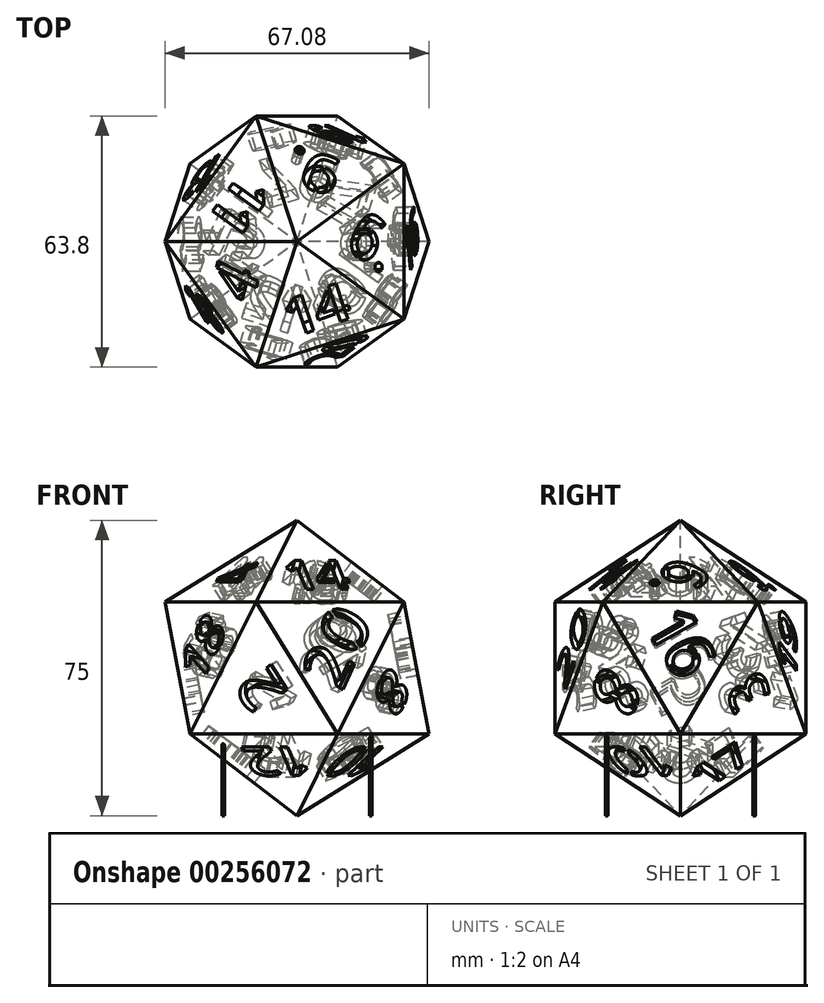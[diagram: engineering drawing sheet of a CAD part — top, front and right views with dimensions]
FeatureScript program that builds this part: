
annotation { "Feature Type Name" : "Feature", "Feature Type Description" : "" }
export const myFeature = defineFeature(function(context is Context, id is Id, definition is map)
    precondition{}
    {
        {
            var Q0;
            Q0=qCreatedBy(makeId("Front.planeOp"),FACE);
            var sketch = newSketch(context, id + "F0", { "sketchPlane" : qUnion([Q0])});
            skCircle(sketch, "E0", {"center": v(0, 0) * mm, "radius": 25 * mm, "construction": true});
            skLineSegment(sketch, "E1", {"start": v(0, 25) * mm, "end": v(-22.36, 11.18) * mm});
            skLineSegment(sketch, "E2", {"start": v(-22.36, 11.18) * mm, "end": v(-18.1, -11.18) * mm});
            skLineSegment(sketch, "E3", {"start": v(-18.1, -11.18) * mm, "end": v(0, -25) * mm});
            skLineSegment(sketch, "E4", {"start": v(0, -25) * mm, "end": v(22.36, -11.18) * mm});
            skLineSegment(sketch, "E5", {"start": v(22.36, -11.18) * mm, "end": v(18.1, 11.18) * mm});
            skLineSegment(sketch, "E6", {"start": v(0, 25) * mm, "end": v(18.1, 11.18) * mm});
            skCircle(sketch, "E7", {"center": v(0, 0) * mm, "radius": 15.18 * mm, "construction": true});
            skLineSegment(sketch, "E8", {"start": v(0, 15.18) * mm, "end": v(-13.14, -7.59) * mm, "construction": true});
            skLineSegment(sketch, "E9", {"start": v(-13.14, -7.59) * mm, "end": v(13.14, -7.59) * mm, "construction": true});
            skLineSegment(sketch, "E10", {"start": v(13.14, -7.59) * mm, "end": v(0, 15.18) * mm, "construction": true});
            skLineSegment(sketch, "E11", {"start": v(0, -7.59) * mm, "end": v(0, 15.18) * mm, "construction": true});
            skLineSegment(sketch, "E12", {"start": v(13.14, -7.59) * mm, "end": v(0, 0) * mm, "construction": true});
            skLineSegment(sketch, "E13", {"start": v(0, 0) * mm, "end": v(12.06, 15.79) * mm, "construction": true});
            skLineSegment(sketch, "E14", {"start": v(0, 0) * mm, "end": v(-12.06, 9.21) * mm, "construction": true});
            skLineSegment(sketch, "E15", {"start": v(0, 25) * mm, "end": v(-12.06, 9.21) * mm, "construction": true});
            skSolve(sketch);
        }
        {
            var Q0;
            Q0=sQuery(id+"F0.wireOp",EDGE,"E6");
            var Q1;
            Q1=qCreatedBy(makeId("Front.planeOp"),FACE);
            cPlane(context, id + "F1", {"entities" : qUnion([Q0, Q1]), "cplaneType" : CPlaneType.LINE_ANGLE, "offset" : 25 * mm, "angle" : 90 * degree, "width" : 150 * mm, "height" : 150 * mm});
        }
        {
            var Q0;
            Q0=qCreatedBy(id+"F1.planeOp",FACE);
            var sketch = newSketch(context, id + "F2", { "sketchPlane" : qUnion([Q0])});
            skLineSegment(sketch, "E16", {"start": v(-15.18, 0) * mm, "end": v(7.59, 13.14) * mm});
            skLineSegment(sketch, "E17", {"start": v(7.59, 13.14) * mm, "end": v(7.59, -13.14) * mm});
            skLineSegment(sketch, "E18", {"start": v(7.59, -13.14) * mm, "end": v(-15.18, 0) * mm});
            skSolve(sketch);
        }
        {
            var Q0;
            Q0=qSketchRegion(id+"F2",true);
            var Q1;
            Q1=sQuery(id+"F0.wireOp",VERTEX,"E12.end");
            loft(context, id + "F3", {"sheetProfilesArray" : [{ "sheetProfileEntities" : qUnion([Q0]) }, { "sheetProfileEntities" : qUnion([Q1]) }]});
        }
        {
            var Q0;
            Q0=makeQuery(id+"F3.opLoft","SWEPT_BODY",BODY,{"disambiguationData":[OSD([sQuery(id+"F0.wireOp",VERTEX,"E12.end"),makeQuery(id+"F2.imprint","IMPRINT",FACE,{"disambiguationData":[TD([[makeQuery(id+"F2.imprint","IMPRINT",EDGE,{"derivedFrom":sQuery(id+"F2.wireOp",EDGE,"E16")}),-1.0]])]})])]});
            var Q1;
            {var subQ0=sQuery(id+"F2.wireOp",EDGE,"E17");var subQ1=sQuery(id+"F2.wireOp",EDGE,"E18");var subQ2=sQuery(id+"F2.wireOp",EDGE,"E16");Q1=makeQuery(id+"F3.opLoft","SWEPT_FACE",FACE,{"disambiguationData":[OSD([subQ2,subQ0,subQ1]),TDD([makeQuery(id+"F2.imprint","INTERSECT",VERTEX,{"derivedFrom":[subQ2,subQ0]}),makeQuery(id+"F2.imprint","INTERSECT",VERTEX,{"derivedFrom":[subQ0,subQ1]}),makeQuery(id+"F2.imprint","IMPRINT",EDGE,{"derivedFrom":subQ0})])]});}
            mirror(context, id + "F4", {"entities" : qUnion([Q0]), "mirrorPlane" : qUnion([Q1])});
        }
        {
            var Q0;
            Q0=makeQuery(id+"F4.opPattern","COPY",BODY,{"derivedFrom":makeQuery(id+"F3.opLoft","SWEPT_BODY",BODY,{"disambiguationData":[OSD([sQuery(id+"F0.wireOp",VERTEX,"E12.end"),makeQuery(id+"F2.imprint","IMPRINT",FACE,{"disambiguationData":[TD([[makeQuery(id+"F2.imprint","IMPRINT",EDGE,{"derivedFrom":sQuery(id+"F2.wireOp",EDGE,"E16")}),-1.0]])]})])]}),"instanceName":"1"});
            var Q1;
            {var subQ0=sQuery(id+"F2.wireOp",EDGE,"E16");var subQ1=sQuery(id+"F2.wireOp",EDGE,"E17");var subQ2=sQuery(id+"F2.wireOp",EDGE,"E18");Q1=makeQuery(id+"F4.opPattern","COPY",FACE,{"derivedFrom":makeQuery(id+"F3.opLoft","SWEPT_FACE",FACE,{"disambiguationData":[OSD([subQ0,subQ1,subQ2]),TDD([makeQuery(id+"F2.imprint","INTERSECT",VERTEX,{"derivedFrom":[subQ0,subQ2]}),makeQuery(id+"F2.imprint","INTERSECT",VERTEX,{"derivedFrom":[subQ0,subQ1]}),makeQuery(id+"F2.imprint","IMPRINT",EDGE,{"derivedFrom":subQ0})])]}),"instanceName":"1"});}
            mirror(context, id + "F5", {"entities" : qUnion([Q0]), "mirrorPlane" : qUnion([Q1])});
        }
        {
            var Q0;
            Q0=makeQuery(id+"F4.opPattern","COPY",BODY,{"derivedFrom":makeQuery(id+"F3.opLoft","SWEPT_BODY",BODY,{"disambiguationData":[OSD([sQuery(id+"F0.wireOp",VERTEX,"E12.end"),makeQuery(id+"F2.imprint","IMPRINT",FACE,{"disambiguationData":[TD([[makeQuery(id+"F2.imprint","IMPRINT",EDGE,{"derivedFrom":sQuery(id+"F2.wireOp",EDGE,"E16")}),-1.0]])]})])]}),"instanceName":"1"});
            var Q1;
            Q1=makeQuery(id+"F5.opPattern","COPY",BODY,{"derivedFrom":makeQuery(id+"F4.opPattern","COPY",BODY,{"derivedFrom":makeQuery(id+"F3.opLoft","SWEPT_BODY",BODY,{"disambiguationData":[OSD([sQuery(id+"F0.wireOp",VERTEX,"E12.end"),makeQuery(id+"F2.imprint","IMPRINT",FACE,{"disambiguationData":[TD([[makeQuery(id+"F2.imprint","IMPRINT",EDGE,{"derivedFrom":sQuery(id+"F2.wireOp",EDGE,"E16")}),-1.0]])]})])]}),"instanceName":"1"}),"instanceName":"1"});
            var Q2;
            Q2=makeQuery(id+"F3.opLoft","SWEPT_EDGE",EDGE,{"disambiguationData":[OSD([sQuery(id+"F0.wireOp",VERTEX,"E12.end"),sQuery(id+"F2.wireOp",EDGE,"E16"),sQuery(id+"F2.wireOp",EDGE,"E18")])]});
            circularPattern(context, id + "F6", {"entities" : qUnion([Q0, Q1]), "axis" : qUnion([Q2]), "angle" : 72 * degree, "instanceCount" : 5});
        }
        {
            var Q0;
            Q0=makeQuery(id+"F3.opLoft","SWEPT_BODY",BODY,{"disambiguationData":[OSD([sQuery(id+"F0.wireOp",VERTEX,"E12.end"),makeQuery(id+"F2.imprint","IMPRINT",FACE,{"disambiguationData":[TD([[makeQuery(id+"F2.imprint","IMPRINT",EDGE,{"derivedFrom":sQuery(id+"F2.wireOp",EDGE,"E16")}),-1.0]])]})])]});
            var Q1;
            Q1=makeQuery(id+"F3.opLoft","SWEPT_EDGE",EDGE,{"disambiguationData":[OSD([sQuery(id+"F0.wireOp",VERTEX,"E12.end"),sQuery(id+"F2.wireOp",EDGE,"E16"),sQuery(id+"F2.wireOp",EDGE,"E18")])]});
            circularPattern(context, id + "F7", {"entities" : qUnion([Q0]), "axis" : qUnion([Q1]), "angle" : 72 * degree, "instanceCount" : 5});
        }
        {
            var Q0;
            Q0=makeQuery(id+"F7.opPattern","COPY",BODY,{"derivedFrom":makeQuery(id+"F3.opLoft","SWEPT_BODY",BODY,{"disambiguationData":[OSD([sQuery(id+"F0.wireOp",VERTEX,"E12.end"),makeQuery(id+"F2.imprint","IMPRINT",FACE,{"disambiguationData":[TD([[makeQuery(id+"F2.imprint","IMPRINT",EDGE,{"derivedFrom":sQuery(id+"F2.wireOp",EDGE,"E16")}),-1.0]])]})])]}),"instanceName":"4"});
            var Q1;
            Q1=makeQuery(id+"F3.opLoft","SWEPT_BODY",BODY,{"disambiguationData":[OSD([sQuery(id+"F0.wireOp",VERTEX,"E12.end"),makeQuery(id+"F2.imprint","IMPRINT",FACE,{"disambiguationData":[TD([[makeQuery(id+"F2.imprint","IMPRINT",EDGE,{"derivedFrom":sQuery(id+"F2.wireOp",EDGE,"E16")}),-1.0]])]})])]});
            var Q2;
            Q2=makeQuery(id+"F7.opPattern","COPY",BODY,{"derivedFrom":makeQuery(id+"F3.opLoft","SWEPT_BODY",BODY,{"disambiguationData":[OSD([sQuery(id+"F0.wireOp",VERTEX,"E12.end"),makeQuery(id+"F2.imprint","IMPRINT",FACE,{"disambiguationData":[TD([[makeQuery(id+"F2.imprint","IMPRINT",EDGE,{"derivedFrom":sQuery(id+"F2.wireOp",EDGE,"E16")}),-1.0]])]})])]}),"instanceName":"1"});
            var Q3;
            Q3=makeQuery(id+"F7.opPattern","COPY",BODY,{"derivedFrom":makeQuery(id+"F3.opLoft","SWEPT_BODY",BODY,{"disambiguationData":[OSD([sQuery(id+"F0.wireOp",VERTEX,"E12.end"),makeQuery(id+"F2.imprint","IMPRINT",FACE,{"disambiguationData":[TD([[makeQuery(id+"F2.imprint","IMPRINT",EDGE,{"derivedFrom":sQuery(id+"F2.wireOp",EDGE,"E16")}),-1.0]])]})])]}),"instanceName":"2"});
            var Q4;
            Q4=makeQuery(id+"F7.opPattern","COPY",BODY,{"derivedFrom":makeQuery(id+"F3.opLoft","SWEPT_BODY",BODY,{"disambiguationData":[OSD([sQuery(id+"F0.wireOp",VERTEX,"E12.end"),makeQuery(id+"F2.imprint","IMPRINT",FACE,{"disambiguationData":[TD([[makeQuery(id+"F2.imprint","IMPRINT",EDGE,{"derivedFrom":sQuery(id+"F2.wireOp",EDGE,"E16")}),-1.0]])]})])]}),"instanceName":"3"});
            var Q5;
            Q5=qCreatedBy(makeId("Top.planeOp"),FACE);
            mirror(context, id + "F8", {"entities" : qUnion([Q0, Q1, Q2, Q3, Q4]), "mirrorPlane" : qUnion([Q5])});
        }
        {
            var Q0;
            Q0=makeQuery(id+"F8.opPattern","COPY",BODY,{"derivedFrom":makeQuery(id+"F7.opPattern","COPY",BODY,{"derivedFrom":makeQuery(id+"F3.opLoft","SWEPT_BODY",BODY,{"disambiguationData":[OSD([sQuery(id+"F0.wireOp",VERTEX,"E12.end"),makeQuery(id+"F2.imprint","IMPRINT",FACE,{"disambiguationData":[TD([[makeQuery(id+"F2.imprint","IMPRINT",EDGE,{"derivedFrom":sQuery(id+"F2.wireOp",EDGE,"E16")}),-1.0]])]})])]}),"instanceName":"1"}),"instanceName":"1"});
            var Q1;
            Q1=makeQuery(id+"F8.opPattern","COPY",BODY,{"derivedFrom":makeQuery(id+"F3.opLoft","SWEPT_BODY",BODY,{"disambiguationData":[OSD([sQuery(id+"F0.wireOp",VERTEX,"E12.end"),makeQuery(id+"F2.imprint","IMPRINT",FACE,{"disambiguationData":[TD([[makeQuery(id+"F2.imprint","IMPRINT",EDGE,{"derivedFrom":sQuery(id+"F2.wireOp",EDGE,"E16")}),-1.0]])]})])]}),"instanceName":"1"});
            var Q2;
            Q2=makeQuery(id+"F8.opPattern","COPY",BODY,{"derivedFrom":makeQuery(id+"F7.opPattern","COPY",BODY,{"derivedFrom":makeQuery(id+"F3.opLoft","SWEPT_BODY",BODY,{"disambiguationData":[OSD([sQuery(id+"F0.wireOp",VERTEX,"E12.end"),makeQuery(id+"F2.imprint","IMPRINT",FACE,{"disambiguationData":[TD([[makeQuery(id+"F2.imprint","IMPRINT",EDGE,{"derivedFrom":sQuery(id+"F2.wireOp",EDGE,"E16")}),-1.0]])]})])]}),"instanceName":"4"}),"instanceName":"1"});
            var Q3;
            Q3=makeQuery(id+"F8.opPattern","COPY",BODY,{"derivedFrom":makeQuery(id+"F7.opPattern","COPY",BODY,{"derivedFrom":makeQuery(id+"F3.opLoft","SWEPT_BODY",BODY,{"disambiguationData":[OSD([sQuery(id+"F0.wireOp",VERTEX,"E12.end"),makeQuery(id+"F2.imprint","IMPRINT",FACE,{"disambiguationData":[TD([[makeQuery(id+"F2.imprint","IMPRINT",EDGE,{"derivedFrom":sQuery(id+"F2.wireOp",EDGE,"E16")}),-1.0]])]})])]}),"instanceName":"3"}),"instanceName":"1"});
            var Q4;
            Q4=makeQuery(id+"F8.opPattern","COPY",BODY,{"derivedFrom":makeQuery(id+"F7.opPattern","COPY",BODY,{"derivedFrom":makeQuery(id+"F3.opLoft","SWEPT_BODY",BODY,{"disambiguationData":[OSD([sQuery(id+"F0.wireOp",VERTEX,"E12.end"),makeQuery(id+"F2.imprint","IMPRINT",FACE,{"disambiguationData":[TD([[makeQuery(id+"F2.imprint","IMPRINT",EDGE,{"derivedFrom":sQuery(id+"F2.wireOp",EDGE,"E16")}),-1.0]])]})])]}),"instanceName":"2"}),"instanceName":"1"});
            var Q5;
            Q5=makeQuery(id+"F7.opPattern","COPY",EDGE,{"derivedFrom":makeQuery(id+"F3.opLoft","SWEPT_EDGE",EDGE,{"disambiguationData":[OSD([sQuery(id+"F0.wireOp",VERTEX,"E12.end"),sQuery(id+"F2.wireOp",EDGE,"E16"),sQuery(id+"F2.wireOp",EDGE,"E18")])]}),"instanceName":"1"});
            transform(context, id + "F9", {"entities" : qUnion([Q0, Q1, Q2, Q3, Q4]), "transformType" : TransformType.ROTATION, "transformAxis" : qUnion([Q5]), "angle" : 36 * degree, "makeCopy" : false});
        }
        {
            var Q0;
            Q0=makeQuery(id+"F8.opPattern","COPY",BODY,{"derivedFrom":makeQuery(id+"F7.opPattern","COPY",BODY,{"derivedFrom":makeQuery(id+"F3.opLoft","SWEPT_BODY",BODY,{"disambiguationData":[OSD([sQuery(id+"F0.wireOp",VERTEX,"E12.end"),makeQuery(id+"F2.imprint","IMPRINT",FACE,{"disambiguationData":[TD([[makeQuery(id+"F2.imprint","IMPRINT",EDGE,{"derivedFrom":sQuery(id+"F2.wireOp",EDGE,"E16")}),-1.0]])]})])]}),"instanceName":"1"}),"instanceName":"1"});
            var Q1;
            Q1=makeQuery(id+"F8.opPattern","COPY",BODY,{"derivedFrom":makeQuery(id+"F3.opLoft","SWEPT_BODY",BODY,{"disambiguationData":[OSD([sQuery(id+"F0.wireOp",VERTEX,"E12.end"),makeQuery(id+"F2.imprint","IMPRINT",FACE,{"disambiguationData":[TD([[makeQuery(id+"F2.imprint","IMPRINT",EDGE,{"derivedFrom":sQuery(id+"F2.wireOp",EDGE,"E16")}),-1.0]])]})])]}),"instanceName":"1"});
            var Q2;
            Q2=makeQuery(id+"F7.opPattern","COPY",BODY,{"derivedFrom":makeQuery(id+"F3.opLoft","SWEPT_BODY",BODY,{"disambiguationData":[OSD([sQuery(id+"F0.wireOp",VERTEX,"E12.end"),makeQuery(id+"F2.imprint","IMPRINT",FACE,{"disambiguationData":[TD([[makeQuery(id+"F2.imprint","IMPRINT",EDGE,{"derivedFrom":sQuery(id+"F2.wireOp",EDGE,"E16")}),-1.0]])]})])]}),"instanceName":"2"});
            var Q3;
            Q3=makeQuery(id+"F7.opPattern","COPY",BODY,{"derivedFrom":makeQuery(id+"F3.opLoft","SWEPT_BODY",BODY,{"disambiguationData":[OSD([sQuery(id+"F0.wireOp",VERTEX,"E12.end"),makeQuery(id+"F2.imprint","IMPRINT",FACE,{"disambiguationData":[TD([[makeQuery(id+"F2.imprint","IMPRINT",EDGE,{"derivedFrom":sQuery(id+"F2.wireOp",EDGE,"E16")}),-1.0]])]})])]}),"instanceName":"1"});
            var Q4;
            Q4=makeQuery(id+"F6.opPattern","COPY",BODY,{"derivedFrom":makeQuery(id+"F4.opPattern","COPY",BODY,{"derivedFrom":makeQuery(id+"F3.opLoft","SWEPT_BODY",BODY,{"disambiguationData":[OSD([sQuery(id+"F0.wireOp",VERTEX,"E12.end"),makeQuery(id+"F2.imprint","IMPRINT",FACE,{"disambiguationData":[TD([[makeQuery(id+"F2.imprint","IMPRINT",EDGE,{"derivedFrom":sQuery(id+"F2.wireOp",EDGE,"E16")}),-1.0]])]})])]}),"instanceName":"1"}),"instanceName":"4"});
            var Q5;
            Q5=makeQuery(id+"F6.opPattern","COPY",BODY,{"derivedFrom":makeQuery(id+"F5.opPattern","COPY",BODY,{"derivedFrom":makeQuery(id+"F4.opPattern","COPY",BODY,{"derivedFrom":makeQuery(id+"F3.opLoft","SWEPT_BODY",BODY,{"disambiguationData":[OSD([sQuery(id+"F0.wireOp",VERTEX,"E12.end"),makeQuery(id+"F2.imprint","IMPRINT",FACE,{"disambiguationData":[TD([[makeQuery(id+"F2.imprint","IMPRINT",EDGE,{"derivedFrom":sQuery(id+"F2.wireOp",EDGE,"E16")}),-1.0]])]})])]}),"instanceName":"1"}),"instanceName":"1"}),"instanceName":"3"});
            var Q6;
            Q6=makeQuery(id+"F6.opPattern","COPY",BODY,{"derivedFrom":makeQuery(id+"F5.opPattern","COPY",BODY,{"derivedFrom":makeQuery(id+"F4.opPattern","COPY",BODY,{"derivedFrom":makeQuery(id+"F3.opLoft","SWEPT_BODY",BODY,{"disambiguationData":[OSD([sQuery(id+"F0.wireOp",VERTEX,"E12.end"),makeQuery(id+"F2.imprint","IMPRINT",FACE,{"disambiguationData":[TD([[makeQuery(id+"F2.imprint","IMPRINT",EDGE,{"derivedFrom":sQuery(id+"F2.wireOp",EDGE,"E16")}),-1.0]])]})])]}),"instanceName":"1"}),"instanceName":"1"}),"instanceName":"4"});
            var Q7;
            Q7=makeQuery(id+"F6.opPattern","COPY",BODY,{"derivedFrom":makeQuery(id+"F4.opPattern","COPY",BODY,{"derivedFrom":makeQuery(id+"F3.opLoft","SWEPT_BODY",BODY,{"disambiguationData":[OSD([sQuery(id+"F0.wireOp",VERTEX,"E12.end"),makeQuery(id+"F2.imprint","IMPRINT",FACE,{"disambiguationData":[TD([[makeQuery(id+"F2.imprint","IMPRINT",EDGE,{"derivedFrom":sQuery(id+"F2.wireOp",EDGE,"E16")}),-1.0]])]})])]}),"instanceName":"1"}),"instanceName":"3"});
            var Q8;
            Q8=makeQuery(id+"F7.opPattern","COPY",BODY,{"derivedFrom":makeQuery(id+"F3.opLoft","SWEPT_BODY",BODY,{"disambiguationData":[OSD([sQuery(id+"F0.wireOp",VERTEX,"E12.end"),makeQuery(id+"F2.imprint","IMPRINT",FACE,{"disambiguationData":[TD([[makeQuery(id+"F2.imprint","IMPRINT",EDGE,{"derivedFrom":sQuery(id+"F2.wireOp",EDGE,"E16")}),-1.0]])]})])]}),"instanceName":"3"});
            var Q9;
            Q9=makeQuery(id+"F7.opPattern","COPY",BODY,{"derivedFrom":makeQuery(id+"F3.opLoft","SWEPT_BODY",BODY,{"disambiguationData":[OSD([sQuery(id+"F0.wireOp",VERTEX,"E12.end"),makeQuery(id+"F2.imprint","IMPRINT",FACE,{"disambiguationData":[TD([[makeQuery(id+"F2.imprint","IMPRINT",EDGE,{"derivedFrom":sQuery(id+"F2.wireOp",EDGE,"E16")}),-1.0]])]})])]}),"instanceName":"4"});
            var Q10;
            Q10=makeQuery(id+"F8.opPattern","COPY",BODY,{"derivedFrom":makeQuery(id+"F7.opPattern","COPY",BODY,{"derivedFrom":makeQuery(id+"F3.opLoft","SWEPT_BODY",BODY,{"disambiguationData":[OSD([sQuery(id+"F0.wireOp",VERTEX,"E12.end"),makeQuery(id+"F2.imprint","IMPRINT",FACE,{"disambiguationData":[TD([[makeQuery(id+"F2.imprint","IMPRINT",EDGE,{"derivedFrom":sQuery(id+"F2.wireOp",EDGE,"E16")}),-1.0]])]})])]}),"instanceName":"2"}),"instanceName":"1"});
            var Q11;
            Q11=makeQuery(id+"F5.opPattern","COPY",BODY,{"derivedFrom":makeQuery(id+"F4.opPattern","COPY",BODY,{"derivedFrom":makeQuery(id+"F3.opLoft","SWEPT_BODY",BODY,{"disambiguationData":[OSD([sQuery(id+"F0.wireOp",VERTEX,"E12.end"),makeQuery(id+"F2.imprint","IMPRINT",FACE,{"disambiguationData":[TD([[makeQuery(id+"F2.imprint","IMPRINT",EDGE,{"derivedFrom":sQuery(id+"F2.wireOp",EDGE,"E16")}),-1.0]])]})])]}),"instanceName":"1"}),"instanceName":"1"});
            var Q12;
            Q12=makeQuery(id+"F4.opPattern","COPY",BODY,{"derivedFrom":makeQuery(id+"F3.opLoft","SWEPT_BODY",BODY,{"disambiguationData":[OSD([sQuery(id+"F0.wireOp",VERTEX,"E12.end"),makeQuery(id+"F2.imprint","IMPRINT",FACE,{"disambiguationData":[TD([[makeQuery(id+"F2.imprint","IMPRINT",EDGE,{"derivedFrom":sQuery(id+"F2.wireOp",EDGE,"E16")}),-1.0]])]})])]}),"instanceName":"1"});
            var Q13;
            Q13=makeQuery(id+"F6.opPattern","COPY",BODY,{"derivedFrom":makeQuery(id+"F4.opPattern","COPY",BODY,{"derivedFrom":makeQuery(id+"F3.opLoft","SWEPT_BODY",BODY,{"disambiguationData":[OSD([sQuery(id+"F0.wireOp",VERTEX,"E12.end"),makeQuery(id+"F2.imprint","IMPRINT",FACE,{"disambiguationData":[TD([[makeQuery(id+"F2.imprint","IMPRINT",EDGE,{"derivedFrom":sQuery(id+"F2.wireOp",EDGE,"E16")}),-1.0]])]})])]}),"instanceName":"1"}),"instanceName":"1"});
            var Q14;
            Q14=makeQuery(id+"F3.opLoft","SWEPT_BODY",BODY,{"disambiguationData":[OSD([sQuery(id+"F0.wireOp",VERTEX,"E12.end"),makeQuery(id+"F2.imprint","IMPRINT",FACE,{"disambiguationData":[TD([[makeQuery(id+"F2.imprint","IMPRINT",EDGE,{"derivedFrom":sQuery(id+"F2.wireOp",EDGE,"E16")}),-1.0]])]})])]});
            var Q15;
            Q15=makeQuery(id+"F6.opPattern","COPY",BODY,{"derivedFrom":makeQuery(id+"F5.opPattern","COPY",BODY,{"derivedFrom":makeQuery(id+"F4.opPattern","COPY",BODY,{"derivedFrom":makeQuery(id+"F3.opLoft","SWEPT_BODY",BODY,{"disambiguationData":[OSD([sQuery(id+"F0.wireOp",VERTEX,"E12.end"),makeQuery(id+"F2.imprint","IMPRINT",FACE,{"disambiguationData":[TD([[makeQuery(id+"F2.imprint","IMPRINT",EDGE,{"derivedFrom":sQuery(id+"F2.wireOp",EDGE,"E16")}),-1.0]])]})])]}),"instanceName":"1"}),"instanceName":"1"}),"instanceName":"1"});
            var Q16;
            Q16=makeQuery(id+"F6.opPattern","COPY",BODY,{"derivedFrom":makeQuery(id+"F5.opPattern","COPY",BODY,{"derivedFrom":makeQuery(id+"F4.opPattern","COPY",BODY,{"derivedFrom":makeQuery(id+"F3.opLoft","SWEPT_BODY",BODY,{"disambiguationData":[OSD([sQuery(id+"F0.wireOp",VERTEX,"E12.end"),makeQuery(id+"F2.imprint","IMPRINT",FACE,{"disambiguationData":[TD([[makeQuery(id+"F2.imprint","IMPRINT",EDGE,{"derivedFrom":sQuery(id+"F2.wireOp",EDGE,"E16")}),-1.0]])]})])]}),"instanceName":"1"}),"instanceName":"1"}),"instanceName":"2"});
            var Q17;
            Q17=makeQuery(id+"F6.opPattern","COPY",BODY,{"derivedFrom":makeQuery(id+"F4.opPattern","COPY",BODY,{"derivedFrom":makeQuery(id+"F3.opLoft","SWEPT_BODY",BODY,{"disambiguationData":[OSD([sQuery(id+"F0.wireOp",VERTEX,"E12.end"),makeQuery(id+"F2.imprint","IMPRINT",FACE,{"disambiguationData":[TD([[makeQuery(id+"F2.imprint","IMPRINT",EDGE,{"derivedFrom":sQuery(id+"F2.wireOp",EDGE,"E16")}),-1.0]])]})])]}),"instanceName":"1"}),"instanceName":"2"});
            var Q18;
            Q18=makeQuery(id+"F8.opPattern","COPY",BODY,{"derivedFrom":makeQuery(id+"F7.opPattern","COPY",BODY,{"derivedFrom":makeQuery(id+"F3.opLoft","SWEPT_BODY",BODY,{"disambiguationData":[OSD([sQuery(id+"F0.wireOp",VERTEX,"E12.end"),makeQuery(id+"F2.imprint","IMPRINT",FACE,{"disambiguationData":[TD([[makeQuery(id+"F2.imprint","IMPRINT",EDGE,{"derivedFrom":sQuery(id+"F2.wireOp",EDGE,"E16")}),-1.0]])]})])]}),"instanceName":"3"}),"instanceName":"1"});
            var Q19;
            Q19=makeQuery(id+"F8.opPattern","COPY",BODY,{"derivedFrom":makeQuery(id+"F7.opPattern","COPY",BODY,{"derivedFrom":makeQuery(id+"F3.opLoft","SWEPT_BODY",BODY,{"disambiguationData":[OSD([sQuery(id+"F0.wireOp",VERTEX,"E12.end"),makeQuery(id+"F2.imprint","IMPRINT",FACE,{"disambiguationData":[TD([[makeQuery(id+"F2.imprint","IMPRINT",EDGE,{"derivedFrom":sQuery(id+"F2.wireOp",EDGE,"E16")}),-1.0]])]})])]}),"instanceName":"4"}),"instanceName":"1"});
            booleanBodies(context, id + "F10", {"operationType" : BooleanOperationType.UNION, "tools" : qUnion([Q0, Q1, Q2, Q3, Q4, Q5, Q6, Q7, Q8, Q9, Q10, Q11, Q12, Q13, Q14, Q15, Q16, Q17, Q18, Q19])});
        }
        {
            var Q0;
            Q0=makeQuery(id+"F6.opPattern","COPY",FACE,{"derivedFrom":makeQuery(id+"F4.opPattern","COPY",FACE,{"derivedFrom":makeQuery(id+"F3.opLoft","CAP_FACE",FACE,{"disambiguationData":[OSD([makeQuery(id+"F2.imprint","IMPRINT",FACE,{"disambiguationData":[TD([[makeQuery(id+"F2.imprint","IMPRINT",EDGE,{"derivedFrom":sQuery(id+"F2.wireOp",EDGE,"E16")}),-1.0]])]})])],"isStart":true}),"instanceName":"1"}),"instanceName":"1"});
            var sketch = newSketch(context, id + "F11", { "sketchPlane" : qUnion([Q0])});
            skText(sketch, "E19", { "text": "20", "fontName": "AllertaStencil-Regular.ttf"});
            const initialGuessF11  = {"E19": [0.00142, -0.00821, 0.42262, 0.9063, 0.008]};
            skSetInitialGuess(sketch, initialGuessF11);
            skSolve(sketch);
        }
        {
            var Q0;
            Q0 = qSketchRegion(id + "F11", true);
            extrude(context, id + "F12", {"entities" : qUnion([Q0]), "operationType" : NewBodyOperationType.REMOVE, "oppositeDirection" : true, "depth" : 3 * mm});
        }
        {
            var Q0;
            Q0=makeQuery(id+"F6.opPattern","COPY",FACE,{"derivedFrom":makeQuery(id+"F5.opPattern","COPY",FACE,{"derivedFrom":makeQuery(id+"F4.opPattern","COPY",FACE,{"derivedFrom":makeQuery(id+"F3.opLoft","CAP_FACE",FACE,{"disambiguationData":[OSD([makeQuery(id+"F2.imprint","IMPRINT",FACE,{"disambiguationData":[TD([[makeQuery(id+"F2.imprint","IMPRINT",EDGE,{"derivedFrom":sQuery(id+"F2.wireOp",EDGE,"E16")}),-1.0]])]})])],"isStart":true}),"instanceName":"1"}),"instanceName":"1"}),"instanceName":"2"});
            var sketch = newSketch(context, id + "F13", { "sketchPlane" : qUnion([Q0])});
            skText(sketch, "E20", { "text": "2", "fontName": "AllertaStencil-Regular.ttf"});
            const initialGuessF13  = {"E20": [0.00513, -0.00035, -0.57358, 0.81915, 0.008]};
            skSetInitialGuess(sketch, initialGuessF13);
            skSolve(sketch);
        }
        {
            var Q0;
            Q0 = qSketchRegion(id + "F13", true);
            extrude(context, id + "F14", {"entities" : qUnion([Q0]), "operationType" : NewBodyOperationType.REMOVE, "oppositeDirection" : true, "depth" : 3 * mm});
        }
        {
            var Q0;
            Q0=makeQuery(id+"F7.opPattern","COPY",FACE,{"derivedFrom":makeQuery(id+"F3.opLoft","CAP_FACE",FACE,{"disambiguationData":[OSD([makeQuery(id+"F2.imprint","IMPRINT",FACE,{"disambiguationData":[TD([[makeQuery(id+"F2.imprint","IMPRINT",EDGE,{"derivedFrom":sQuery(id+"F2.wireOp",EDGE,"E16")}),-1.0]])]})])],"isStart":true}),"instanceName":"1"});
            var sketch = newSketch(context, id + "F15", { "sketchPlane" : qUnion([Q0])});
            skText(sketch, "E21", { "text": "14", "fontName": "AllertaStencil-Regular.ttf"});
            const initialGuessF15  = {"E21": [-0.00445, -0.00533, 0.96593, 0.25882, 0.008]};
            skSetInitialGuess(sketch, initialGuessF15);
            skSolve(sketch);
        }
        {
            var Q0;
            Q0 = qSketchRegion(id + "F15", true);
            extrude(context, id + "F16", {"entities" : qUnion([Q0]), "operationType" : NewBodyOperationType.REMOVE, "oppositeDirection" : true, "depth" : 3 * mm});
        }
        {
            var Q0;
            Q0=makeQuery(id+"F6.opPattern","COPY",FACE,{"derivedFrom":makeQuery(id+"F5.opPattern","COPY",FACE,{"derivedFrom":makeQuery(id+"F4.opPattern","COPY",FACE,{"derivedFrom":makeQuery(id+"F3.opLoft","CAP_FACE",FACE,{"disambiguationData":[OSD([makeQuery(id+"F2.imprint","IMPRINT",FACE,{"disambiguationData":[TD([[makeQuery(id+"F2.imprint","IMPRINT",EDGE,{"derivedFrom":sQuery(id+"F2.wireOp",EDGE,"E16")}),-1.0]])]})])],"isStart":true}),"instanceName":"1"}),"instanceName":"1"}),"instanceName":"1"});
            var sketch = newSketch(context, id + "F17", { "sketchPlane" : qUnion([Q0])});
            skText(sketch, "E22", { "text": "8", "fontName": "AllertaStencil-Regular.ttf"});
            const initialGuessF17  = {"E22": [-0.00198, 0.00483, -0.3842, -0.92325, 0.009]};
            skSetInitialGuess(sketch, initialGuessF17);
            skSolve(sketch);
        }
        {
            var Q0;
            Q0 = qSketchRegion(id + "F17", true);
            extrude(context, id + "F18", {"entities" : qUnion([Q0]), "operationType" : NewBodyOperationType.REMOVE, "oppositeDirection" : true, "depth" : 3 * mm});
        }
        {
            var Q0;
            Q0=makeQuery(id+"F6.opPattern","COPY",FACE,{"derivedFrom":makeQuery(id+"F4.opPattern","COPY",FACE,{"derivedFrom":makeQuery(id+"F3.opLoft","CAP_FACE",FACE,{"disambiguationData":[OSD([makeQuery(id+"F2.imprint","IMPRINT",FACE,{"disambiguationData":[TD([[makeQuery(id+"F2.imprint","IMPRINT",EDGE,{"derivedFrom":sQuery(id+"F2.wireOp",EDGE,"E16")}),-1.0]])]})])],"isStart":true}),"instanceName":"1"}),"instanceName":"2"});
            var sketch = newSketch(context, id + "F19", { "sketchPlane" : qUnion([Q0])});
            skText(sketch, "E23", { "text": "18", "fontName": "AllertaStencil-Regular.ttf"});
            const initialGuessF19  = {"E23": [0.0016, -0.00667, 0.37864, 0.92554, 0.008]};
            skSetInitialGuess(sketch, initialGuessF19);
            skSolve(sketch);
        }
        {
            var Q0;
            Q0 = qSketchRegion(id + "F19", true);
            extrude(context, id + "F20", {"entities" : qUnion([Q0]), "operationType" : NewBodyOperationType.REMOVE, "oppositeDirection" : true, "depth" : 3 * mm});
        }
        {
            var Q0;
            Q0=makeQuery(id+"F7.opPattern","COPY",FACE,{"derivedFrom":makeQuery(id+"F3.opLoft","CAP_FACE",FACE,{"disambiguationData":[OSD([makeQuery(id+"F2.imprint","IMPRINT",FACE,{"disambiguationData":[TD([[makeQuery(id+"F2.imprint","IMPRINT",EDGE,{"derivedFrom":sQuery(id+"F2.wireOp",EDGE,"E16")}),-1.0]])]})])],"isStart":true}),"instanceName":"2"});
            var sketch = newSketch(context, id + "F21", { "sketchPlane" : qUnion([Q0])});
            skText(sketch, "E24", { "text": "4", "fontName": "AllertaStencil-Regular.ttf"});
            const initialGuessF21  = {"E24": [0.00224, -0.00386, 0.25882, 0.96593, 0.008]};
            skSetInitialGuess(sketch, initialGuessF21);
            skSolve(sketch);
        }
        {
            var Q0;
            Q0 = qSketchRegion(id + "F21", true);
            extrude(context, id + "F22", {"entities" : qUnion([Q0]), "operationType" : NewBodyOperationType.REMOVE, "oppositeDirection" : true, "depth" : 3 * mm});
        }
        {
            var Q0;
            Q0=makeQuery(id+"F6.opPattern","COPY",FACE,{"derivedFrom":makeQuery(id+"F5.opPattern","COPY",FACE,{"derivedFrom":makeQuery(id+"F4.opPattern","COPY",FACE,{"derivedFrom":makeQuery(id+"F3.opLoft","CAP_FACE",FACE,{"disambiguationData":[OSD([makeQuery(id+"F2.imprint","IMPRINT",FACE,{"disambiguationData":[TD([[makeQuery(id+"F2.imprint","IMPRINT",EDGE,{"derivedFrom":sQuery(id+"F2.wireOp",EDGE,"E16")}),-1.0]])]})])],"isStart":true}),"instanceName":"1"}),"instanceName":"1"}),"instanceName":"3"});
            var sketch = newSketch(context, id + "F23", { "sketchPlane" : qUnion([Q0])});
            skText(sketch, "E25", { "text": "5", "fontName": "DroidSansMono.ttf"});
            const initialGuessF23  = {"E25": [-0.00207, 0.0048, -0.46217, -0.8868, 0.009]};
            skSetInitialGuess(sketch, initialGuessF23);
            skSolve(sketch);
        }
        {
            var Q0;
            Q0 = qSketchRegion(id + "F23", true);
            extrude(context, id + "F24", {"entities" : qUnion([Q0]), "operationType" : NewBodyOperationType.REMOVE, "oppositeDirection" : true, "depth" : 3 * mm});
        }
        {
            var Q0;
            Q0=makeQuery(id+"F8.opPattern","COPY",FACE,{"derivedFrom":makeQuery(id+"F7.opPattern","COPY",FACE,{"derivedFrom":makeQuery(id+"F3.opLoft","CAP_FACE",FACE,{"disambiguationData":[OSD([makeQuery(id+"F2.imprint","IMPRINT",FACE,{"disambiguationData":[TD([[makeQuery(id+"F2.imprint","IMPRINT",EDGE,{"derivedFrom":sQuery(id+"F2.wireOp",EDGE,"E16")}),-1.0]])]})])],"isStart":true}),"instanceName":"2"}),"instanceName":"1"});
            var sketch = newSketch(context, id + "F25", { "sketchPlane" : qUnion([Q0])});
            skText(sketch, "E26", { "text": "15", "fontName": "OpenSans-Bold.ttf"});
            const initialGuessF25  = {"E26": [-0.00359, -0.00683, 0.86603, 0.5, 0.008]};
            skSetInitialGuess(sketch, initialGuessF25);
            skSolve(sketch);
        }
        {
            var Q0;
            Q0 = qSketchRegion(id + "F25", true);
            extrude(context, id + "F26", {"entities" : qUnion([Q0]), "operationType" : NewBodyOperationType.REMOVE, "oppositeDirection" : true, "depth" : 3 * mm});
        }
        {
            var Q0;
            Q0=makeQuery(id+"F8.opPattern","COPY",FACE,{"derivedFrom":makeQuery(id+"F7.opPattern","COPY",FACE,{"derivedFrom":makeQuery(id+"F3.opLoft","CAP_FACE",FACE,{"disambiguationData":[OSD([makeQuery(id+"F2.imprint","IMPRINT",FACE,{"disambiguationData":[TD([[makeQuery(id+"F2.imprint","IMPRINT",EDGE,{"derivedFrom":sQuery(id+"F2.wireOp",EDGE,"E16")}),-1.0]])]})])],"isStart":true}),"instanceName":"1"}),"instanceName":"1"});
            var sketch = newSketch(context, id + "F27", { "sketchPlane" : qUnion([Q0])});
            skText(sketch, "E27", { "text": "12", "fontName": "AllertaStencil-Regular.ttf"});
            const initialGuessF27  = {"E27": [0.0044, 0.00532, -0.96593, -0.25882, 0.008]};
            skSetInitialGuess(sketch, initialGuessF27);
            skSolve(sketch);
        }
        {
            var Q0;
            Q0 = qSketchRegion(id + "F27", true);
            extrude(context, id + "F28", {"entities" : qUnion([Q0]), "operationType" : NewBodyOperationType.REMOVE, "oppositeDirection" : true, "depth" : 3 * mm});
        }
        {
            var Q0;
            Q0=makeQuery(id+"F8.opPattern","COPY",FACE,{"derivedFrom":makeQuery(id+"F3.opLoft","CAP_FACE",FACE,{"disambiguationData":[OSD([makeQuery(id+"F2.imprint","IMPRINT",FACE,{"disambiguationData":[TD([[makeQuery(id+"F2.imprint","IMPRINT",EDGE,{"derivedFrom":sQuery(id+"F2.wireOp",EDGE,"E16")}),-1.0]])]})])],"isStart":true}),"instanceName":"1"});
            var sketch = newSketch(context, id + "F29", { "sketchPlane" : qUnion([Q0])});
            skText(sketch, "E28", { "text": "10", "fontName": "AllertaStencil-Regular.ttf"});
            const initialGuessF29  = {"E28": [0.00709, -0.00182, -0.6756, 0.73728, 0.008]};
            skSetInitialGuess(sketch, initialGuessF29);
            skSolve(sketch);
        }
        {
            var Q0;
            Q0 = qSketchRegion(id + "F29", true);
            extrude(context, id + "F30", {"entities" : qUnion([Q0]), "operationType" : NewBodyOperationType.REMOVE, "oppositeDirection" : true, "depth" : 3 * mm});
        }
        {
            var Q0;
            Q0=makeQuery(id+"F8.opPattern","COPY",FACE,{"derivedFrom":makeQuery(id+"F7.opPattern","COPY",FACE,{"derivedFrom":makeQuery(id+"F3.opLoft","CAP_FACE",FACE,{"disambiguationData":[OSD([makeQuery(id+"F2.imprint","IMPRINT",FACE,{"disambiguationData":[TD([[makeQuery(id+"F2.imprint","IMPRINT",EDGE,{"derivedFrom":sQuery(id+"F2.wireOp",EDGE,"E16")}),-1.0]])]})])],"isStart":true}),"instanceName":"4"}),"instanceName":"1"});
            var sketch = newSketch(context, id + "F31", { "sketchPlane" : qUnion([Q0])});
            skText(sketch, "E29", { "text": "17", "fontName": "AllertaStencil-Regular.ttf"});
            const initialGuessF31  = {"E29": [-0.00639, 0.00406, 0.3007, -0.95372, 0.008]};
            skSetInitialGuess(sketch, initialGuessF31);
            skSolve(sketch);
        }
        {
            var Q0;
            Q0 = qSketchRegion(id + "F31", true);
            extrude(context, id + "F32", {"entities" : qUnion([Q0]), "operationType" : NewBodyOperationType.REMOVE, "oppositeDirection" : true, "depth" : 3 * mm});
        }
        {
            var Q0;
            Q0=makeQuery(id+"F5.opPattern","COPY",FACE,{"derivedFrom":makeQuery(id+"F4.opPattern","COPY",FACE,{"derivedFrom":makeQuery(id+"F3.opLoft","CAP_FACE",FACE,{"disambiguationData":[OSD([makeQuery(id+"F2.imprint","IMPRINT",FACE,{"disambiguationData":[TD([[makeQuery(id+"F2.imprint","IMPRINT",EDGE,{"derivedFrom":sQuery(id+"F2.wireOp",EDGE,"E16")}),-1.0]])]})])],"isStart":true}),"instanceName":"1"}),"instanceName":"1"});
            var sketch = newSketch(context, id + "F33", { "sketchPlane" : qUnion([Q0])});
            skText(sketch, "E30", { "text": "3", "fontName": "AllertaStencil-Regular.ttf"});
            const initialGuessF33  = {"E30": [0.00488, -0.00185, -0.37946, 0.9252, 0.008]};
            skSetInitialGuess(sketch, initialGuessF33);
            skSolve(sketch);
        }
        {
            var Q0;
            Q0 = qSketchRegion(id + "F33", true);
            extrude(context, id + "F34", {"entities" : qUnion([Q0]), "operationType" : NewBodyOperationType.REMOVE, "oppositeDirection" : true, "depth" : 3 * mm});
        }
        {
            var Q0;
            Q0=makeQuery(id+"F4.opPattern","COPY",FACE,{"derivedFrom":makeQuery(id+"F3.opLoft","CAP_FACE",FACE,{"disambiguationData":[OSD([makeQuery(id+"F2.imprint","IMPRINT",FACE,{"disambiguationData":[TD([[makeQuery(id+"F2.imprint","IMPRINT",EDGE,{"derivedFrom":sQuery(id+"F2.wireOp",EDGE,"E16")}),-1.0]])]})])],"isStart":true}),"instanceName":"1"});
            var sketch = newSketch(context, id + "F35", { "sketchPlane" : qUnion([Q0])});
            skText(sketch, "E31", { "text": "16", "fontName": "AllertaStencil-Regular.ttf"});
            const initialGuessF35  = {"E31": [-0.00598, 0.00335, 0.5, -0.86603, 0.008]};
            skSetInitialGuess(sketch, initialGuessF35);
            skSolve(sketch);
        }
        {
            var Q0;
            Q0 = qSketchRegion(id + "F35", true);
            extrude(context, id + "F36", {"entities" : qUnion([Q0]), "operationType" : NewBodyOperationType.REMOVE, "oppositeDirection" : true, "depth" : 3 * mm});
        }
        {
            var Q0;
            Q0=makeQuery(id+"F3.opLoft","CAP_FACE",FACE,{"disambiguationData":[OSD([makeQuery(id+"F2.imprint","IMPRINT",FACE,{"disambiguationData":[TD([[makeQuery(id+"F2.imprint","IMPRINT",EDGE,{"derivedFrom":sQuery(id+"F2.wireOp",EDGE,"E16")}),-1.0]])]})])],"isStart":true});
            var sketch = newSketch(context, id + "F37", { "sketchPlane" : qUnion([Q0])});
            skText(sketch, "E32", { "text": "6.", "fontName": "AllertaStencil-Regular.ttf"});
            const initialGuessF37  = {"E32": [-0.0052, -0.00093, 0.86603, -0.5, 0.008]};
            skSetInitialGuess(sketch, initialGuessF37);
            skSolve(sketch);
        }
        {
            var Q0;
            Q0 = qSketchRegion(id + "F37", true);
            extrude(context, id + "F38", {"entities" : qUnion([Q0]), "operationType" : NewBodyOperationType.REMOVE, "oppositeDirection" : true, "depth" : 3 * mm});
        }
        {
            var Q0;
            Q0=makeQuery(id+"F6.opPattern","COPY",FACE,{"derivedFrom":makeQuery(id+"F4.opPattern","COPY",FACE,{"derivedFrom":makeQuery(id+"F3.opLoft","CAP_FACE",FACE,{"disambiguationData":[OSD([makeQuery(id+"F2.imprint","IMPRINT",FACE,{"disambiguationData":[TD([[makeQuery(id+"F2.imprint","IMPRINT",EDGE,{"derivedFrom":sQuery(id+"F2.wireOp",EDGE,"E16")}),-1.0]])]})])],"isStart":true}),"instanceName":"1"}),"instanceName":"4"});
            var sketch = newSketch(context, id + "F39", { "sketchPlane" : qUnion([Q0])});
            skText(sketch, "E33", { "text": "19", "fontName": "AllertaStencil-Regular.ttf"});
            const initialGuessF39  = {"E33": [-0.00053, -0.00635, 0.5373, 0.8434, 0.008]};
            skSetInitialGuess(sketch, initialGuessF39);
            skSolve(sketch);
        }
        {
            var Q0;
            Q0 = qSketchRegion(id + "F39", true);
            extrude(context, id + "F40", {"entities" : qUnion([Q0]), "operationType" : NewBodyOperationType.REMOVE, "oppositeDirection" : true, "depth" : 3 * mm});
        }
        {
            var Q0;
            Q0=makeQuery(id+"F7.opPattern","COPY",FACE,{"derivedFrom":makeQuery(id+"F3.opLoft","CAP_FACE",FACE,{"disambiguationData":[OSD([makeQuery(id+"F2.imprint","IMPRINT",FACE,{"disambiguationData":[TD([[makeQuery(id+"F2.imprint","IMPRINT",EDGE,{"derivedFrom":sQuery(id+"F2.wireOp",EDGE,"E16")}),-1.0]])]})])],"isStart":true}),"instanceName":"4"});
            var sketch = newSketch(context, id + "F41", { "sketchPlane" : qUnion([Q0])});
            skText(sketch, "E34", { "text": "9.", "fontName": "AllertaStencil-Regular.ttf"});
            const initialGuessF41  = {"E34": [0.00473, 0.00312, -0.96825, 0.25, 0.008]};
            skSetInitialGuess(sketch, initialGuessF41);
            skSolve(sketch);
        }
        {
            var Q0;
            Q0 = qSketchRegion(id + "F41", true);
            extrude(context, id + "F42", {"entities" : qUnion([Q0]), "operationType" : NewBodyOperationType.REMOVE, "oppositeDirection" : true, "depth" : 3 * mm});
        }
        {
            var Q0;
            Q0=makeQuery(id+"F7.opPattern","COPY",FACE,{"derivedFrom":makeQuery(id+"F3.opLoft","CAP_FACE",FACE,{"disambiguationData":[OSD([makeQuery(id+"F2.imprint","IMPRINT",FACE,{"disambiguationData":[TD([[makeQuery(id+"F2.imprint","IMPRINT",EDGE,{"derivedFrom":sQuery(id+"F2.wireOp",EDGE,"E16")}),-1.0]])]})])],"isStart":true}),"instanceName":"3"});
            var sketch = newSketch(context, id + "F43", { "sketchPlane" : qUnion([Q0])});
            skText(sketch, "E35", { "text": "11", "fontName": "AllertaStencil-Regular.ttf"});
            const initialGuessF43  = {"E35": [0.0004, 0.00509, -0.67477, -0.73803, 0.008]};
            skSetInitialGuess(sketch, initialGuessF43);
            skSolve(sketch);
        }
        {
            var Q0;
            Q0 = qSketchRegion(id + "F43", true);
            extrude(context, id + "F44", {"entities" : qUnion([Q0]), "operationType" : NewBodyOperationType.REMOVE, "oppositeDirection" : true, "depth" : 3 * mm});
        }
        {
            var Q0;
            Q0=makeQuery(id+"F6.opPattern","COPY",FACE,{"derivedFrom":makeQuery(id+"F4.opPattern","COPY",FACE,{"derivedFrom":makeQuery(id+"F3.opLoft","CAP_FACE",FACE,{"disambiguationData":[OSD([makeQuery(id+"F2.imprint","IMPRINT",FACE,{"disambiguationData":[TD([[makeQuery(id+"F2.imprint","IMPRINT",EDGE,{"derivedFrom":sQuery(id+"F2.wireOp",EDGE,"E16")}),-1.0]])]})])],"isStart":true}),"instanceName":"1"}),"instanceName":"3"});
            var sketch = newSketch(context, id + "F45", { "sketchPlane" : qUnion([Q0])});
            skText(sketch, "E36", { "text": "13", "fontName": "AllertaStencil-Regular.ttf"});
            const initialGuessF45  = {"E36": [-0.00498, 0.00375, 0.37847, -0.92561, 0.008]};
            skSetInitialGuess(sketch, initialGuessF45);
            skSolve(sketch);
        }
        {
            var Q0;
            Q0 = qSketchRegion(id + "F45", true);
            extrude(context, id + "F46", {"entities" : qUnion([Q0]), "operationType" : NewBodyOperationType.REMOVE, "oppositeDirection" : true, "depth" : 3 * mm});
        }
        {
            var Q0;
            Q0=makeQuery(id+"F8.opPattern","COPY",FACE,{"derivedFrom":makeQuery(id+"F7.opPattern","COPY",FACE,{"derivedFrom":makeQuery(id+"F3.opLoft","CAP_FACE",FACE,{"disambiguationData":[OSD([makeQuery(id+"F2.imprint","IMPRINT",FACE,{"disambiguationData":[TD([[makeQuery(id+"F2.imprint","IMPRINT",EDGE,{"derivedFrom":sQuery(id+"F2.wireOp",EDGE,"E16")}),-1.0]])]})])],"isStart":true}),"instanceName":"3"}),"instanceName":"1"});
            var sketch = newSketch(context, id + "F47", { "sketchPlane" : qUnion([Q0])});
            skText(sketch, "E37", { "text": "7", "fontName": "AllertaStencil-Regular.ttf"});
            const initialGuessF47  = {"E37": [-0.00398, -0.00276, 0.96825, -0.25, 0.008]};
            skSetInitialGuess(sketch, initialGuessF47);
            skSolve(sketch);
        }
        {
            var Q0;
            Q0 = qSketchRegion(id + "F47", true);
            extrude(context, id + "F48", {"entities" : qUnion([Q0]), "operationType" : NewBodyOperationType.REMOVE, "oppositeDirection" : true, "depth" : 3 * mm});
        }
        {
            var Q0;
            Q0=makeQuery(id+"F6.opPattern","COPY",FACE,{"derivedFrom":makeQuery(id+"F5.opPattern","COPY",FACE,{"derivedFrom":makeQuery(id+"F4.opPattern","COPY",FACE,{"derivedFrom":makeQuery(id+"F3.opLoft","CAP_FACE",FACE,{"disambiguationData":[OSD([makeQuery(id+"F2.imprint","IMPRINT",FACE,{"disambiguationData":[TD([[makeQuery(id+"F2.imprint","IMPRINT",EDGE,{"derivedFrom":sQuery(id+"F2.wireOp",EDGE,"E16")}),-1.0]])]})])],"isStart":true}),"instanceName":"1"}),"instanceName":"1"}),"instanceName":"4"});
            var sketch = newSketch(context, id + "F49", { "sketchPlane" : qUnion([Q0])});
            skText(sketch, "E38", { "text": "1", "fontName": "AllertaStencil-Regular.ttf"});
            const initialGuessF49  = {"E38": [0.0035, -0.00086, -0.44639, 0.89484, 0.008]};
            skSetInitialGuess(sketch, initialGuessF49);
            skSolve(sketch);
        }
        {
            var Q0;
            Q0 = qSketchRegion(id + "F49", true);
            extrude(context, id + "F50", {"entities" : qUnion([Q0]), "operationType" : NewBodyOperationType.REMOVE, "oppositeDirection" : true, "depth" : 3 * mm});
        }
        {
            var Q0;
            Q0=qCreatedBy(makeId("Top.planeOp"),FACE);
            cPlane(context, id + "F51", {"entities" : qUnion([Q0]), "cplaneType" : CPlaneType.OFFSET, "offset" : 25 * mm, "oppositeDirection" : true, "width" : 150 * mm, "height" : 150 * mm});
        }
        {
            var Q0;
            Q0=qCreatedBy(id+"F51.planeOp",FACE);
            var sketch = newSketch(context, id + "F52", { "sketchPlane" : qUnion([Q0])});
            skLineSegment(sketch, "E39.bottom", {"start": v(12.5, 12.5) * mm, "end": v(-12.5, 12.5) * mm});
            skLineSegment(sketch, "E39.top", {"start": v(12.5, -12.5) * mm, "end": v(-12.5, -12.5) * mm});
            skLineSegment(sketch, "E39.left", {"start": v(12.5, 12.5) * mm, "end": v(12.5, -12.5) * mm});
            skLineSegment(sketch, "E39.right", {"start": v(-12.5, 12.5) * mm, "end": v(-12.5, -12.5) * mm});
            skPoint(sketch, "E39.middle", {"position": v(0, 0) * mm});
            skCircle(sketch, "E40", {"center": v(12.5, -12.5) * mm, "radius": 0.2 * mm});
            skCircle(sketch, "E41", {"center": v(-12.5, -12.5) * mm, "radius": 0.2 * mm});
            skCircle(sketch, "E42", {"center": v(12.5, 12.5) * mm, "radius": 0.2 * mm});
            skCircle(sketch, "E43", {"center": v(-12.5, 12.5) * mm, "radius": 0.2 * mm});
            skSolve(sketch);
        }
        {
            var Q0;
            {var subQ0=sQuery(id+"F52.wireOp",EDGE,"E39.right");var subQ1=sQuery(id+"F52.wireOp",EDGE,"E39.top");var subQ2=makeQuery(id+"F52.imprint","INTERSECT",VERTEX,{"derivedFrom":[subQ1,subQ0]});Q0=makeQuery(id+"F52.imprint","IMPRINT",FACE,{"disambiguationData":[TD([[makeQuery(id+"F52.imprint","IMPRINT",EDGE,{"disambiguationData":[TD([[subQ2,1.0]])],"derivedFrom":subQ1}),1.0]])]});}
            var Q1;
            {var subQ0=sQuery(id+"F52.wireOp",EDGE,"E39.left");var subQ1=sQuery(id+"F52.wireOp",EDGE,"E39.top");var subQ2=makeQuery(id+"F52.imprint","INTERSECT",VERTEX,{"derivedFrom":[subQ1,subQ0]});Q1=makeQuery(id+"F52.imprint","IMPRINT",FACE,{"disambiguationData":[TD([[makeQuery(id+"F52.imprint","IMPRINT",EDGE,{"disambiguationData":[TD([[subQ2,-1.0]])],"derivedFrom":subQ1}),-1.0]])]});}
            var Q2;
            {var subQ0=sQuery(id+"F52.wireOp",EDGE,"E39.left");var subQ1=sQuery(id+"F52.wireOp",EDGE,"E39.top");var subQ2=makeQuery(id+"F52.imprint","INTERSECT",VERTEX,{"derivedFrom":[subQ1,subQ0]});Q2=makeQuery(id+"F52.imprint","IMPRINT",FACE,{"disambiguationData":[TD([[makeQuery(id+"F52.imprint","IMPRINT",EDGE,{"disambiguationData":[TD([[subQ2,-1.0]])],"derivedFrom":subQ1}),1.0]])]});}
            var Q3;
            {var subQ0=sQuery(id+"F52.wireOp",EDGE,"E39.right");var subQ1=sQuery(id+"F52.wireOp",EDGE,"E39.top");var subQ2=makeQuery(id+"F52.imprint","INTERSECT",VERTEX,{"derivedFrom":[subQ1,subQ0]});Q3=makeQuery(id+"F52.imprint","IMPRINT",FACE,{"disambiguationData":[TD([[makeQuery(id+"F52.imprint","IMPRINT",EDGE,{"disambiguationData":[TD([[subQ2,1.0]])],"derivedFrom":subQ1}),-1.0]])]});}
            var Q4;
            {var subQ0=sQuery(id+"F52.wireOp",EDGE,"E39.right");var subQ1=sQuery(id+"F52.wireOp",EDGE,"E39.bottom");var subQ2=makeQuery(id+"F52.imprint","INTERSECT",VERTEX,{"derivedFrom":[subQ1,subQ0]});Q4=makeQuery(id+"F52.imprint","IMPRINT",FACE,{"disambiguationData":[TD([[makeQuery(id+"F52.imprint","IMPRINT",EDGE,{"disambiguationData":[TD([[subQ2,1.0]])],"derivedFrom":subQ1}),-1.0]])]});}
            var Q5;
            {var subQ0=sQuery(id+"F52.wireOp",EDGE,"E39.right");var subQ1=sQuery(id+"F52.wireOp",EDGE,"E39.bottom");var subQ2=makeQuery(id+"F52.imprint","INTERSECT",VERTEX,{"derivedFrom":[subQ1,subQ0]});Q5=makeQuery(id+"F52.imprint","IMPRINT",FACE,{"disambiguationData":[TD([[makeQuery(id+"F52.imprint","IMPRINT",EDGE,{"disambiguationData":[TD([[subQ2,1.0]])],"derivedFrom":subQ1}),1.0]])]});}
            var Q6;
            {var subQ0=sQuery(id+"F52.wireOp",EDGE,"E39.left");var subQ1=sQuery(id+"F52.wireOp",EDGE,"E39.bottom");var subQ2=makeQuery(id+"F52.imprint","INTERSECT",VERTEX,{"derivedFrom":[subQ1,subQ0]});Q6=makeQuery(id+"F52.imprint","IMPRINT",FACE,{"disambiguationData":[TD([[makeQuery(id+"F52.imprint","IMPRINT",EDGE,{"disambiguationData":[TD([[subQ2,-1.0]])],"derivedFrom":subQ1}),1.0]])]});}
            var Q7;
            {var subQ0=sQuery(id+"F52.wireOp",EDGE,"E39.left");var subQ1=sQuery(id+"F52.wireOp",EDGE,"E39.bottom");var subQ2=makeQuery(id+"F52.imprint","INTERSECT",VERTEX,{"derivedFrom":[subQ1,subQ0]});Q7=makeQuery(id+"F52.imprint","IMPRINT",FACE,{"disambiguationData":[TD([[makeQuery(id+"F52.imprint","IMPRINT",EDGE,{"disambiguationData":[TD([[subQ2,-1.0]])],"derivedFrom":subQ1}),-1.0]])]});}
            var Q8;
            Q8=sQuery(id+"F52.wireOp",EDGE,"E40");
            var Q9;
            Q9=sQuery(id+"F52.wireOp",EDGE,"E41");
            var Q10;
            Q10=sQuery(id+"F52.wireOp",EDGE,"E43");
            var Q11;
            Q11=sQuery(id+"F52.wireOp",EDGE,"E42");
            extrude(context, id + "F53", {"entities" : qUnion([Q0, Q1, Q2, Q3, Q4, Q5, Q6, Q7]), "surfaceEntities" : qUnion([Q8, Q9, Q10, Q11]), "endBound" : BoundingType.UP_TO_NEXT, "depth" : 25 * mm});
        }
        {
            var Q0;
            Q0=makeQuery(id+"F8.opPattern","COPY",BODY,{"derivedFrom":makeQuery(id+"F7.opPattern","COPY",BODY,{"derivedFrom":makeQuery(id+"F3.opLoft","SWEPT_BODY",BODY,{"disambiguationData":[OSD([sQuery(id+"F0.wireOp",VERTEX,"E12.end"),makeQuery(id+"F2.imprint","IMPRINT",FACE,{"disambiguationData":[TD([[makeQuery(id+"F2.imprint","IMPRINT",EDGE,{"derivedFrom":sQuery(id+"F2.wireOp",EDGE,"E16")}),-1.0]])]})])]}),"instanceName":"1"}),"instanceName":"1"});
            var Q1;
            Q1=makeQuery(id+"F53.opExtrude","SWEPT_BODY",BODY,{"disambiguationData":[OSD([sQuery(id+"F52.wireOp",EDGE,"E40")])]});
            var Q2;
            Q2=makeQuery(id+"F53.opExtrude","SWEPT_BODY",BODY,{"disambiguationData":[OSD([sQuery(id+"F52.wireOp",EDGE,"E42")])]});
            var Q3;
            Q3=makeQuery(id+"F53.opExtrude","SWEPT_BODY",BODY,{"disambiguationData":[OSD([sQuery(id+"F52.wireOp",EDGE,"E41")])]});
            var Q4;
            Q4=makeQuery(id+"F53.opExtrude","SWEPT_BODY",BODY,{"disambiguationData":[OSD([sQuery(id+"F52.wireOp",EDGE,"E43")])]});
            var Q5;
            Q5=qCreatedBy(makeId("Origin.pointOp"),VERTEX);
            transform(context, id + "F54", {"entities" : qUnion([Q0, Q1, Q2, Q3, Q4]), "transformType" : TransformType.SCALE_UNIFORMLY, "scale" : 1.5, "scalePoint" : qUnion([Q5]), "makeCopy" : false});
        }
    });
